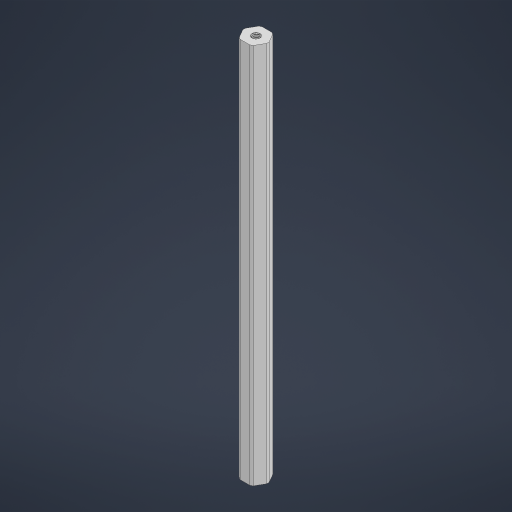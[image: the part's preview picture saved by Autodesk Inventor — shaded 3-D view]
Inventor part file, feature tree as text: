
AUTODESK INVENTOR PART (.ipt)
format: ipt  version: 2023 (Build 270158000, 158)  size: 755,712 bytes
history: native  units: in
note: dims shown in document units (in); Inventor stores cm internally (conversion verified against a paired STEP export)
features: mirror x1
ambient origin geometry x8: Origin, YZ Plane, XZ Plane, XY Plane, X Axis, Y Axis, Z Axis, Center Point
bodies: Solid1 (feature_tree)
feature tree (1):
  mirror  "Mirror2"
